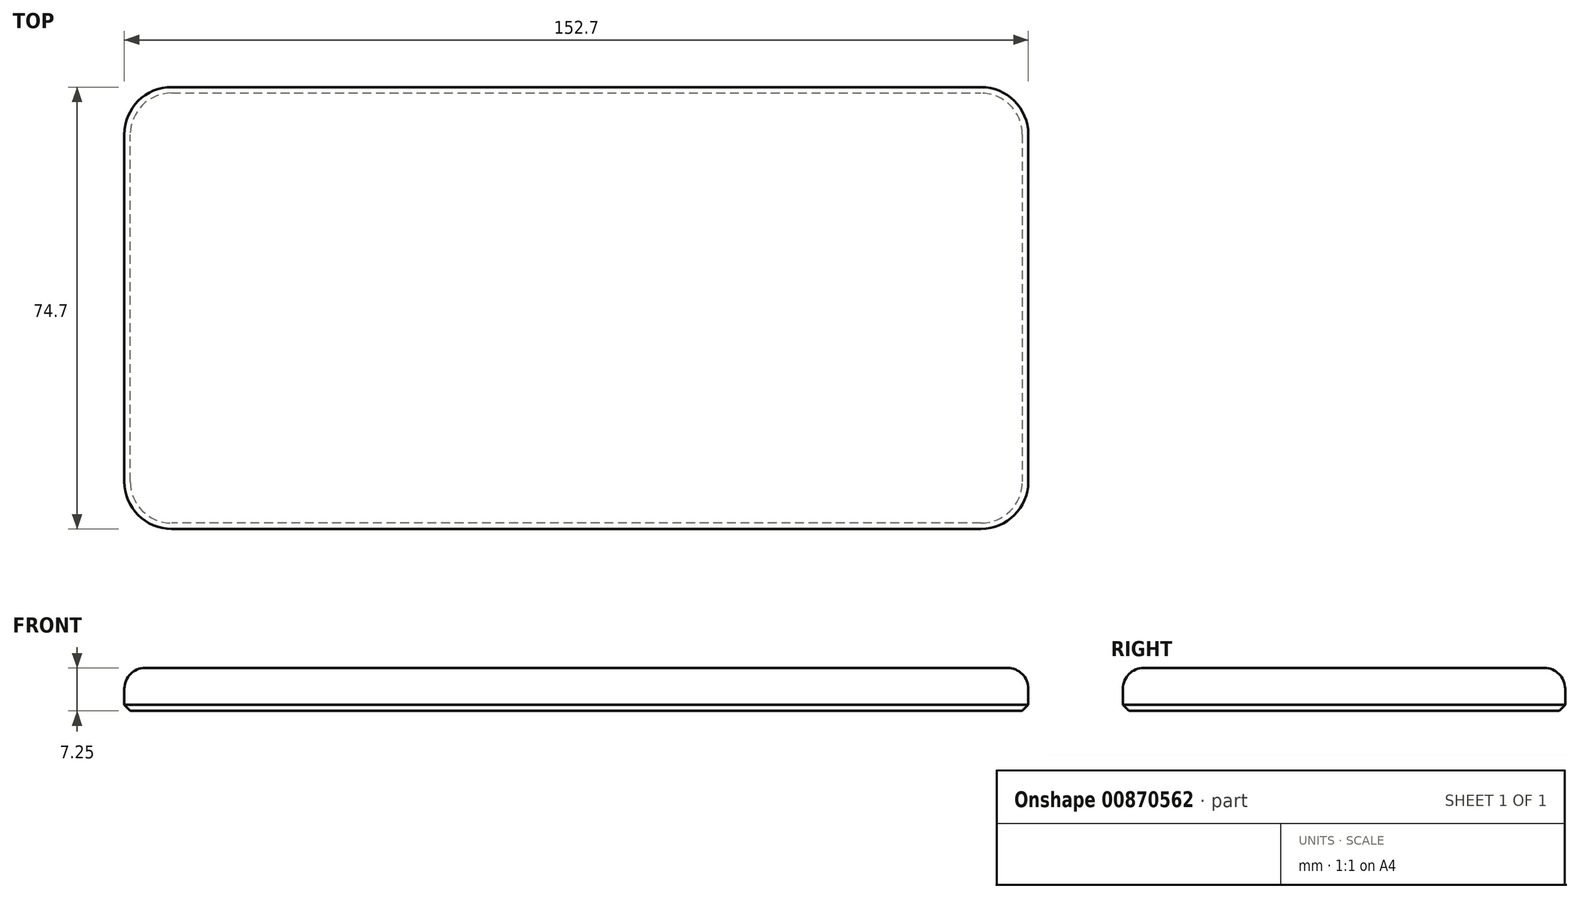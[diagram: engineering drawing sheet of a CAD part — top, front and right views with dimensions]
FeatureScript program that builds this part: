
annotation { "Feature Type Name" : "Feature", "Feature Type Description" : "" }
export const myFeature = defineFeature(function(context is Context, id is Id, definition is map)
    precondition{}
    {
        {
            var Q0;
            Q0=qCreatedBy(makeId("Top.planeOp"),FACE);
            var sketch = newSketch(context, id + "F0", { "sketchPlane" : qUnion([Q0])});
            skLineSegment(sketch, "E0.bottom", {"start": v(76.35, 37.35) * mm, "end": v(-76.35, 37.35) * mm});
            skLineSegment(sketch, "E0.top", {"start": v(76.35, -37.35) * mm, "end": v(-76.35, -37.35) * mm});
            skLineSegment(sketch, "E0.left", {"start": v(76.35, 37.35) * mm, "end": v(76.35, -37.35) * mm});
            skLineSegment(sketch, "E0.right", {"start": v(-76.35, 37.35) * mm, "end": v(-76.35, -37.35) * mm});
            skPoint(sketch, "E0.middle", {"position": v(0, 0) * mm});
            skSolve(sketch);
        }
        {
            var Q0;
            Q0 = qSketchRegion(id + "F0", true);
            var Q1;
            Q1=makeQuery(id+"F0.imprint","IMPRINT",FACE,{"disambiguationData":[TD([[makeQuery(id+"F0.imprint","IMPRINT",EDGE,{"derivedFrom":sQuery(id+"F0.wireOp",EDGE,"E0.bottom")}),1.0]])]});
            extrude(context, id + "F1", {"entities" : qUnion([Q0, Q1]), "depth" : 7.25 * mm, "offsetDistance" : 25 * mm});
        }
        {
            var Q0;
            Q0=makeQuery(id+"F1.opExtrude","SWEPT_EDGE",EDGE,{"disambiguationData":[OSD([sQuery(id+"F0.wireOp",EDGE,"E0.top"),sQuery(id+"F0.wireOp",EDGE,"E0.right")])]});
            var Q1;
            Q1=makeQuery(id+"F1.opExtrude","SWEPT_EDGE",EDGE,{"disambiguationData":[OSD([sQuery(id+"F0.wireOp",EDGE,"E0.top"),sQuery(id+"F0.wireOp",EDGE,"E0.left")])]});
            var Q2;
            Q2=makeQuery(id+"F1.opExtrude","SWEPT_EDGE",EDGE,{"disambiguationData":[OSD([sQuery(id+"F0.wireOp",EDGE,"E0.bottom"),sQuery(id+"F0.wireOp",EDGE,"E0.left")])]});
            var Q3;
            Q3=makeQuery(id+"F1.opExtrude","SWEPT_EDGE",EDGE,{"disambiguationData":[OSD([sQuery(id+"F0.wireOp",EDGE,"E0.bottom"),sQuery(id+"F0.wireOp",EDGE,"E0.right")])]});
            fillet(context, id + "F2", {"entities" : qUnion([Q0, Q1, Q2, Q3]), "radius" : 8 * mm, "tangentPropagation" : true, "allowEdgeOverflow" : false});
        }
        {
            var Q0;
            Q0=makeQuery(id+"F1.opExtrude","CAP_EDGE",EDGE,{"disambiguationData":[OSD([sQuery(id+"F0.wireOp",EDGE,"E0.top")])],"isStart":true});
            var Q1;
            {var subQ0=sQuery(id+"F0.wireOp",EDGE,"E0.left");var subQ1=sQuery(id+"F0.wireOp",EDGE,"E0.top");Q1=makeQuery(id+"F2.opFillet","BLEND_EDGE",EDGE,{"blendedFrom":[makeQuery(id+"F1.opExtrude","SWEPT_EDGE",EDGE,{"disambiguationData":[OSD([subQ1,subQ0])]}),makeQuery(id+"F1.opExtrude","CAP_FACE",FACE,{"disambiguationData":[OSD([sQuery(id+"F0.wireOp",EDGE,"E0.bottom"),subQ1,subQ0,sQuery(id+"F0.wireOp",EDGE,"E0.right")])],"isStart":true})],"blendedInto":[makeQuery(id+"F1.opExtrude","CAP_FACE",FACE,{"disambiguationData":[OSD([sQuery(id+"F0.wireOp",EDGE,"E0.bottom"),subQ1,subQ0,sQuery(id+"F0.wireOp",EDGE,"E0.right")])],"isStart":true})]});}
            var Q2;
            Q2=makeQuery(id+"F1.opExtrude","CAP_EDGE",EDGE,{"disambiguationData":[OSD([sQuery(id+"F0.wireOp",EDGE,"E0.left")])],"isStart":true});
            var Q3;
            {var subQ0=sQuery(id+"F0.wireOp",EDGE,"E0.left");var subQ1=sQuery(id+"F0.wireOp",EDGE,"E0.bottom");Q3=makeQuery(id+"F2.opFillet","BLEND_EDGE",EDGE,{"blendedFrom":[makeQuery(id+"F1.opExtrude","SWEPT_EDGE",EDGE,{"disambiguationData":[OSD([subQ1,subQ0])]}),makeQuery(id+"F1.opExtrude","CAP_FACE",FACE,{"disambiguationData":[OSD([subQ1,sQuery(id+"F0.wireOp",EDGE,"E0.top"),subQ0,sQuery(id+"F0.wireOp",EDGE,"E0.right")])],"isStart":true})],"blendedInto":[makeQuery(id+"F1.opExtrude","CAP_FACE",FACE,{"disambiguationData":[OSD([subQ1,sQuery(id+"F0.wireOp",EDGE,"E0.top"),subQ0,sQuery(id+"F0.wireOp",EDGE,"E0.right")])],"isStart":true})]});}
            var Q4;
            {var subQ0=sQuery(id+"F0.wireOp",EDGE,"E0.right");var subQ1=sQuery(id+"F0.wireOp",EDGE,"E0.top");Q4=makeQuery(id+"F2.opFillet","BLEND_EDGE",EDGE,{"blendedFrom":[makeQuery(id+"F1.opExtrude","SWEPT_EDGE",EDGE,{"disambiguationData":[OSD([subQ1,subQ0])]}),makeQuery(id+"F1.opExtrude","CAP_FACE",FACE,{"disambiguationData":[OSD([sQuery(id+"F0.wireOp",EDGE,"E0.bottom"),subQ1,sQuery(id+"F0.wireOp",EDGE,"E0.left"),subQ0])],"isStart":true})],"blendedInto":[makeQuery(id+"F1.opExtrude","CAP_FACE",FACE,{"disambiguationData":[OSD([sQuery(id+"F0.wireOp",EDGE,"E0.bottom"),subQ1,sQuery(id+"F0.wireOp",EDGE,"E0.left"),subQ0])],"isStart":true})]});}
            var Q5;
            Q5=makeQuery(id+"F1.opExtrude","CAP_EDGE",EDGE,{"disambiguationData":[OSD([sQuery(id+"F0.wireOp",EDGE,"E0.right")])],"isStart":true});
            var Q6;
            {var subQ0=sQuery(id+"F0.wireOp",EDGE,"E0.right");var subQ1=sQuery(id+"F0.wireOp",EDGE,"E0.bottom");Q6=makeQuery(id+"F2.opFillet","BLEND_EDGE",EDGE,{"blendedFrom":[makeQuery(id+"F1.opExtrude","SWEPT_EDGE",EDGE,{"disambiguationData":[OSD([subQ1,subQ0])]}),makeQuery(id+"F1.opExtrude","CAP_FACE",FACE,{"disambiguationData":[OSD([subQ1,sQuery(id+"F0.wireOp",EDGE,"E0.top"),sQuery(id+"F0.wireOp",EDGE,"E0.left"),subQ0])],"isStart":true})],"blendedInto":[makeQuery(id+"F1.opExtrude","CAP_FACE",FACE,{"disambiguationData":[OSD([subQ1,sQuery(id+"F0.wireOp",EDGE,"E0.top"),sQuery(id+"F0.wireOp",EDGE,"E0.left"),subQ0])],"isStart":true})]});}
            var Q7;
            Q7=makeQuery(id+"F1.opExtrude","CAP_EDGE",EDGE,{"disambiguationData":[OSD([sQuery(id+"F0.wireOp",EDGE,"E0.bottom")])],"isStart":true});
            chamfer(context, id + "F3", {"entities" : qUnion([Q0, Q1, Q2, Q3, Q4, Q5, Q6, Q7]), "width" : 1 * mm, "tangentPropagation" : true});
        }
        {
            var Q0;
            Q0=makeQuery(id+"F1.opExtrude","CAP_EDGE",EDGE,{"disambiguationData":[OSD([sQuery(id+"F0.wireOp",EDGE,"E0.top")])],"isStart":false});
            fillet(context, id + "F4", {"entities" : qUnion([Q0]), "radius" : 3.5 * mm, "tangentPropagation" : true, "allowEdgeOverflow" : false});
        }
    });
